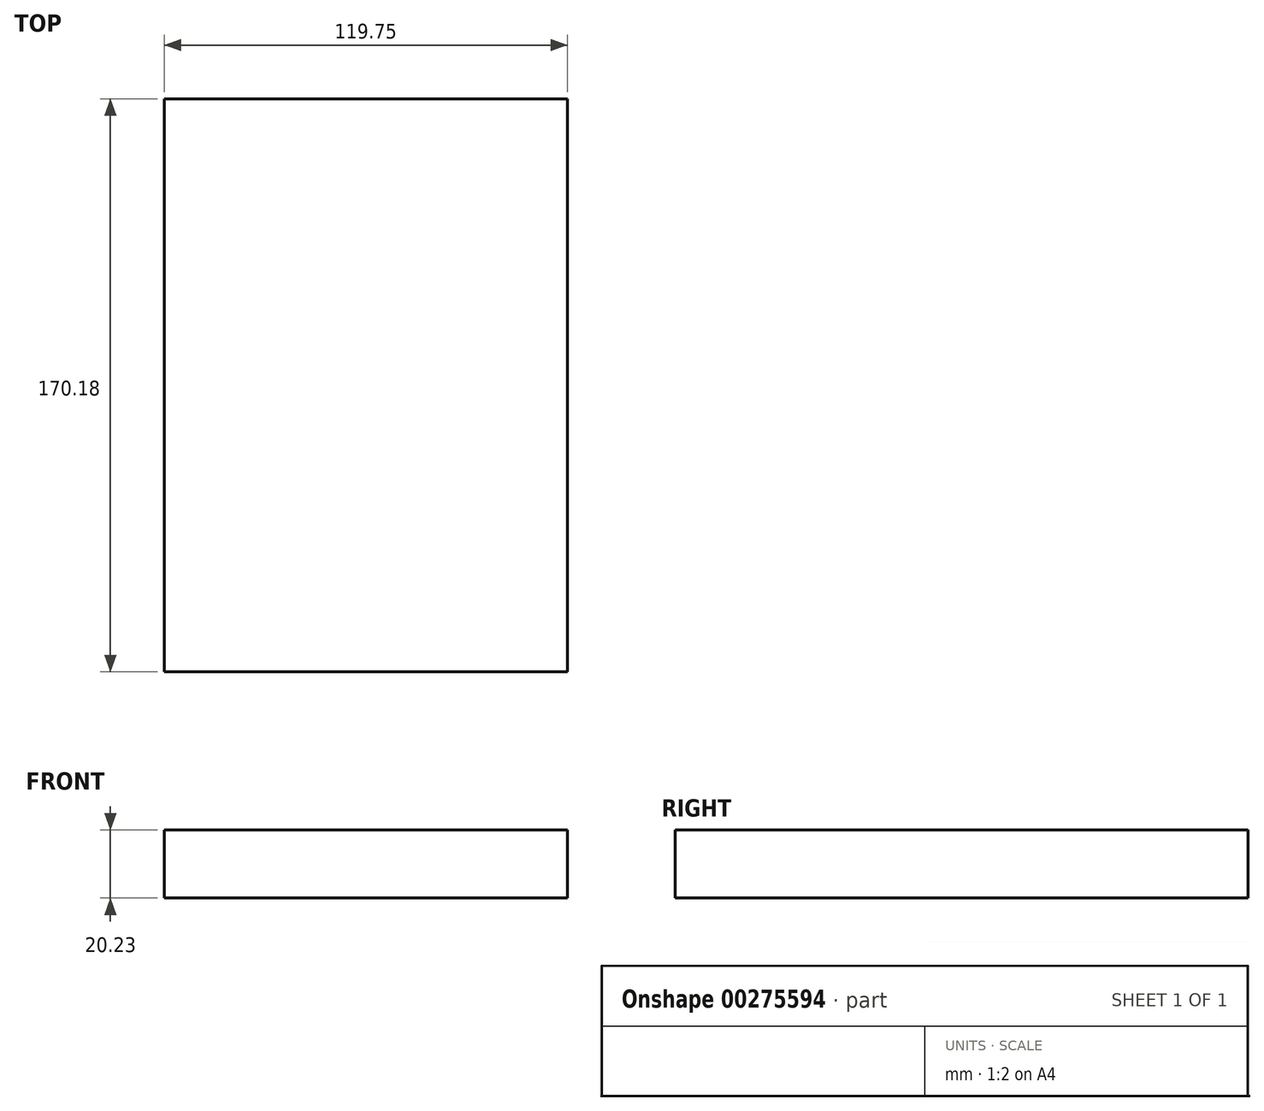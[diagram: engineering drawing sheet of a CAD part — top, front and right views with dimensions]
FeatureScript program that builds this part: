
annotation { "Feature Type Name" : "Feature", "Feature Type Description" : "" }
export const myFeature = defineFeature(function(context is Context, id is Id, definition is map)
    precondition{}
    {
        {
            var Q0;
            Q0=qCreatedBy(makeId("Front.planeOp"),FACE);
            var sketch = newSketch(context, id + "F0", { "sketchPlane" : qUnion([Q0])});
            skLineSegment(sketch, "E0.bottom", {"start": v(-52.39, 20.23) * mm, "end": v(67.36, 20.23) * mm});
            skLineSegment(sketch, "E0.top", {"start": v(-52.39, 0) * mm, "end": v(67.36, 0) * mm});
            skLineSegment(sketch, "E0.left", {"start": v(-52.39, 20.23) * mm, "end": v(-52.39, 0) * mm});
            skLineSegment(sketch, "E0.right", {"start": v(67.36, 20.23) * mm, "end": v(67.36, 0) * mm});
            skSolve(sketch);
        }
        {
            var Q0;
            Q0 = qSketchRegion(id + "F0", true);
            extrude(context, id + "F1", {"entities" : qUnion([Q0]), "depth" : 170.18 * mm});
        }
    });
